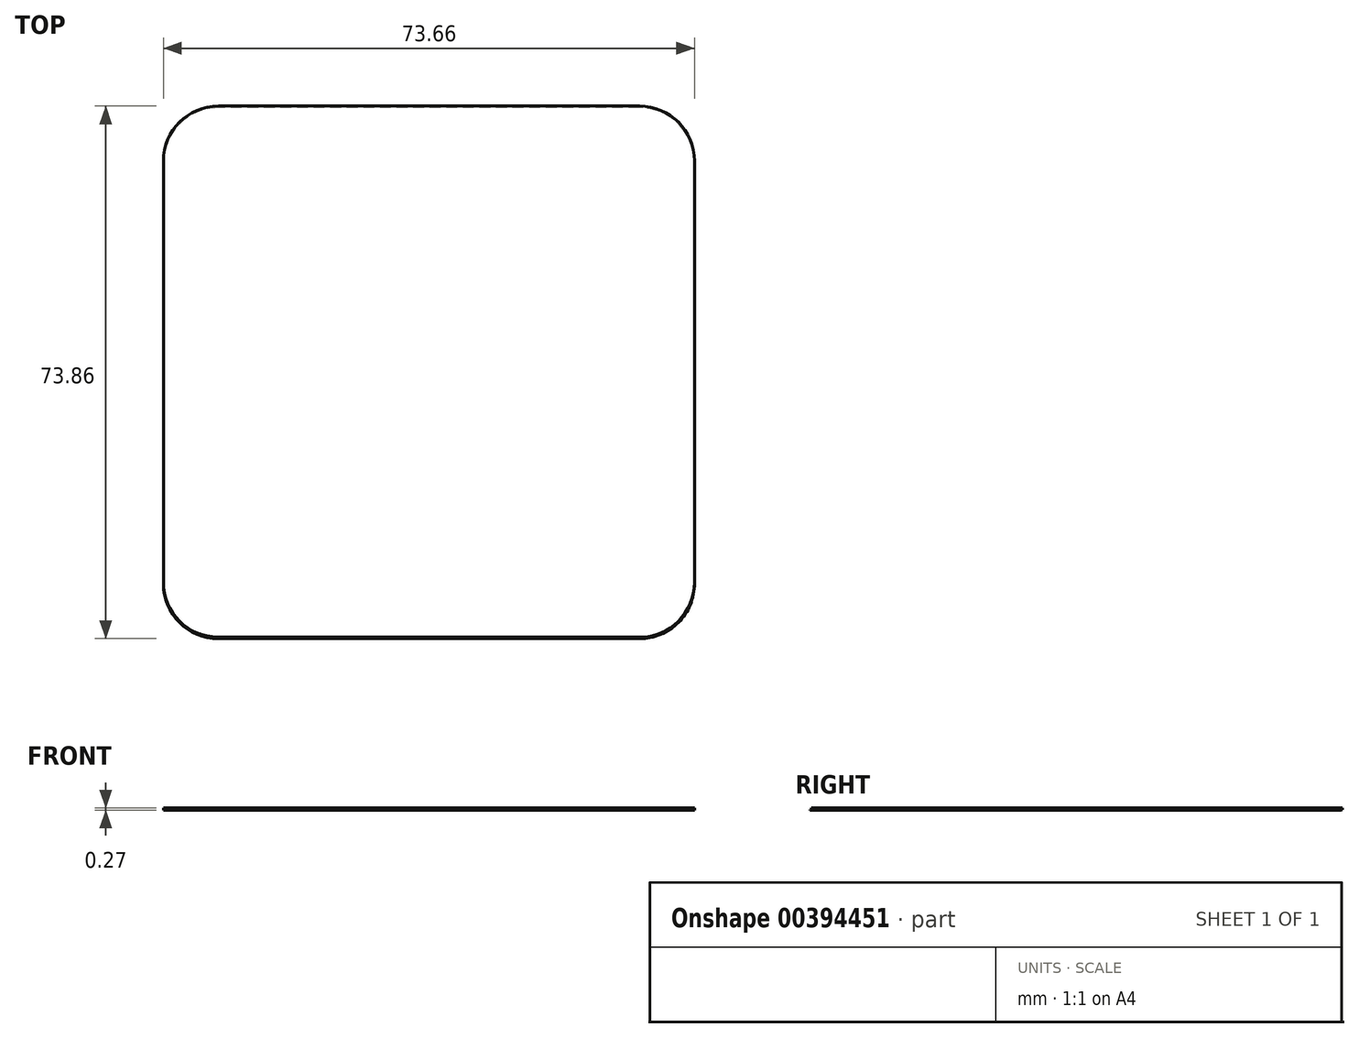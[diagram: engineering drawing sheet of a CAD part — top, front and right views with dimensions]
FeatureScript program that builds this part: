
annotation { "Feature Type Name" : "Feature", "Feature Type Description" : "" }
export const myFeature = defineFeature(function(context is Context, id is Id, definition is map)
    precondition{}
    {
        {
            var Q0;
            Q0=qCreatedBy(makeId("Top.planeOp"),FACE);
            var sketch = newSketch(context, id + "F0", { "sketchPlane" : qUnion([Q0])});
            skLineSegment(sketch, "E0.bottom", {"start": v(29.21, 36.83) * mm, "end": v(-29.2, 36.83) * mm});
            skLineSegment(sketch, "E0.top", {"start": v(29.2, -36.83) * mm, "end": v(-29.2, -36.83) * mm});
            skLineSegment(sketch, "E0.left", {"start": v(36.83, 29.21) * mm, "end": v(36.83, -29.2) * mm});
            skLineSegment(sketch, "E0.right", {"start": v(-36.83, 29.21) * mm, "end": v(-36.83, -29.2) * mm});
            skPoint(sketch, "E0.middle", {"position": v(0, 0) * mm});
            skPoint(sketch, "E1.visualSharp", {"position": v(-36.83, 36.83) * mm});
            skArc(sketch, "E1.filletArc", {"start": v(-29.2, 36.83) * mm, "mid": v(-34.6, 34.6) * mm, "end": v(-36.83, 29.21) * mm});
            skPoint(sketch, "E2.visualSharp", {"position": v(-36.83, -36.83) * mm});
            skArc(sketch, "E2.filletArc", {"start": v(-36.83, -29.2) * mm, "mid": v(-34.6, -34.6) * mm, "end": v(-29.21, -36.83) * mm});
            skPoint(sketch, "E3.visualSharp", {"position": v(36.83, -36.83) * mm});
            skArc(sketch, "E3.filletArc", {"start": v(29.2, -36.83) * mm, "mid": v(34.6, -34.6) * mm, "end": v(36.83, -29.2) * mm});
            skPoint(sketch, "E4.visualSharp", {"position": v(36.83, 36.83) * mm});
            skArc(sketch, "E4.filletArc", {"start": v(36.83, 29.21) * mm, "mid": v(34.6, 34.6) * mm, "end": v(29.21, 36.83) * mm});
            skSolve(sketch);
        }
        {
            var Q0;
            Q0 = qSketchRegion(id + "F0", true);
            extrude(context, id + "F1", {"entities" : qUnion([Q0]), "depth" : 3 / 203.2 * mm});
        }
        {
            var Q0;
            Q0=makeQuery(id+"F1.opExtrude","CAP_FACE",FACE,{"disambiguationData":[OSD([sQuery(id+"F0.wireOp",EDGE,"E0.bottom"),sQuery(id+"F0.wireOp",EDGE,"E0.top"),sQuery(id+"F0.wireOp",EDGE,"E0.left"),sQuery(id+"F0.wireOp",EDGE,"E0.right"),sQuery(id+"F0.wireOp",EDGE,"E1.filletArc"),sQuery(id+"F0.wireOp",EDGE,"E2.filletArc"),sQuery(id+"F0.wireOp",EDGE,"E3.filletArc"),sQuery(id+"F0.wireOp",EDGE,"E4.filletArc")])],"isStart":false});
            var sketch = newSketch(context, id + "F2", { "sketchPlane" : qUnion([Q0])});
            skLineSegment(sketch, "E5.bottom", {"start": v(29.21, 37.03) * mm, "end": v(-29.2, 37.03) * mm});
            skLineSegment(sketch, "E5.top", {"start": v(29.2, -36.63) * mm, "end": v(-29.21, -36.63) * mm});
            skLineSegment(sketch, "E5.left", {"start": v(36.83, 29.4) * mm, "end": v(36.83, -29.01) * mm});
            skLineSegment(sketch, "E5.right", {"start": v(-36.83, 29.4) * mm, "end": v(-36.83, -29.01) * mm});
            skPoint(sketch, "E5.middle", {"position": v(0, 0.2) * mm});
            skPoint(sketch, "E6.visualSharp", {"position": v(-36.83, 37.03) * mm});
            skArc(sketch, "E6.filletArc", {"start": v(-29.2, 37.03) * mm, "mid": v(-34.6, 34.8) * mm, "end": v(-36.83, 29.4) * mm});
            skPoint(sketch, "E7.visualSharp", {"position": v(-36.83, -36.63) * mm});
            skArc(sketch, "E7.filletArc", {"start": v(-36.83, -29.01) * mm, "mid": v(-34.6, -34.4) * mm, "end": v(-29.21, -36.63) * mm});
            skPoint(sketch, "E8.visualSharp", {"position": v(36.83, -36.63) * mm});
            skArc(sketch, "E8.filletArc", {"start": v(29.2, -36.63) * mm, "mid": v(34.6, -34.4) * mm, "end": v(36.83, -29.01) * mm});
            skPoint(sketch, "E9.visualSharp", {"position": v(36.83, 37.03) * mm});
            skArc(sketch, "E9.filletArc", {"start": v(36.83, 29.4) * mm, "mid": v(34.6, 34.8) * mm, "end": v(29.21, 37.03) * mm});
            skSolve(sketch);
        }
        {
            var Q0;
            Q0 = qSketchRegion(id + "F2", true);
            extrude(context, id + "F3", {"entities" : qUnion([Q0]), "operationType" : NewBodyOperationType.ADD, "depth" : 0.25 * mm});
        }
    });
